# Revit family: Fu_Chair_SandlerArum-1-2
name_source: partatom
category: Furniture
units: mm (PartAtom-declared; Revit-internal decimal feet)

## family parameters
Always vertical = Yes
Cut with Voids When Loaded = No
OmniClass Number = 23.40.20.00
OmniClass Title = General Furniture and Specialties
Room Calculation Point = No
Shared = No
Work Plane-Based = No

## types (1)
- Arum 1.2
    Default Elevation = 0 mm  [stored 0 ft]
    Depth = 500 mm  [stored 1.64042 ft]
    Description = Stackable armchair with upholstered seat pad, polypropylene seat and backrest and 4 leg base made with steel tubing. Greenguard Certified.
    Frame = Epoxy - M2_M82
    Height = 765 mm  [stored 2.50984 ft]
    Manufacturer = Sandler
    Model = Arum 1.2
    Polypropylene Back = Polypropylene - M2_M56
    Seat = Fabric - Manhattan - Bronx YI364
    URL = https://www.sandlerseating.com
    Width = 590 mm  [stored 1.9357 ft]

note: [stored X ft] marks values corroborated as IEEE doubles in the binary element streams (Revit-internal decimal feet)

## geometry (parser evidence)
native form markers: Sweep x5
no freeform markers — native parametric forms only
